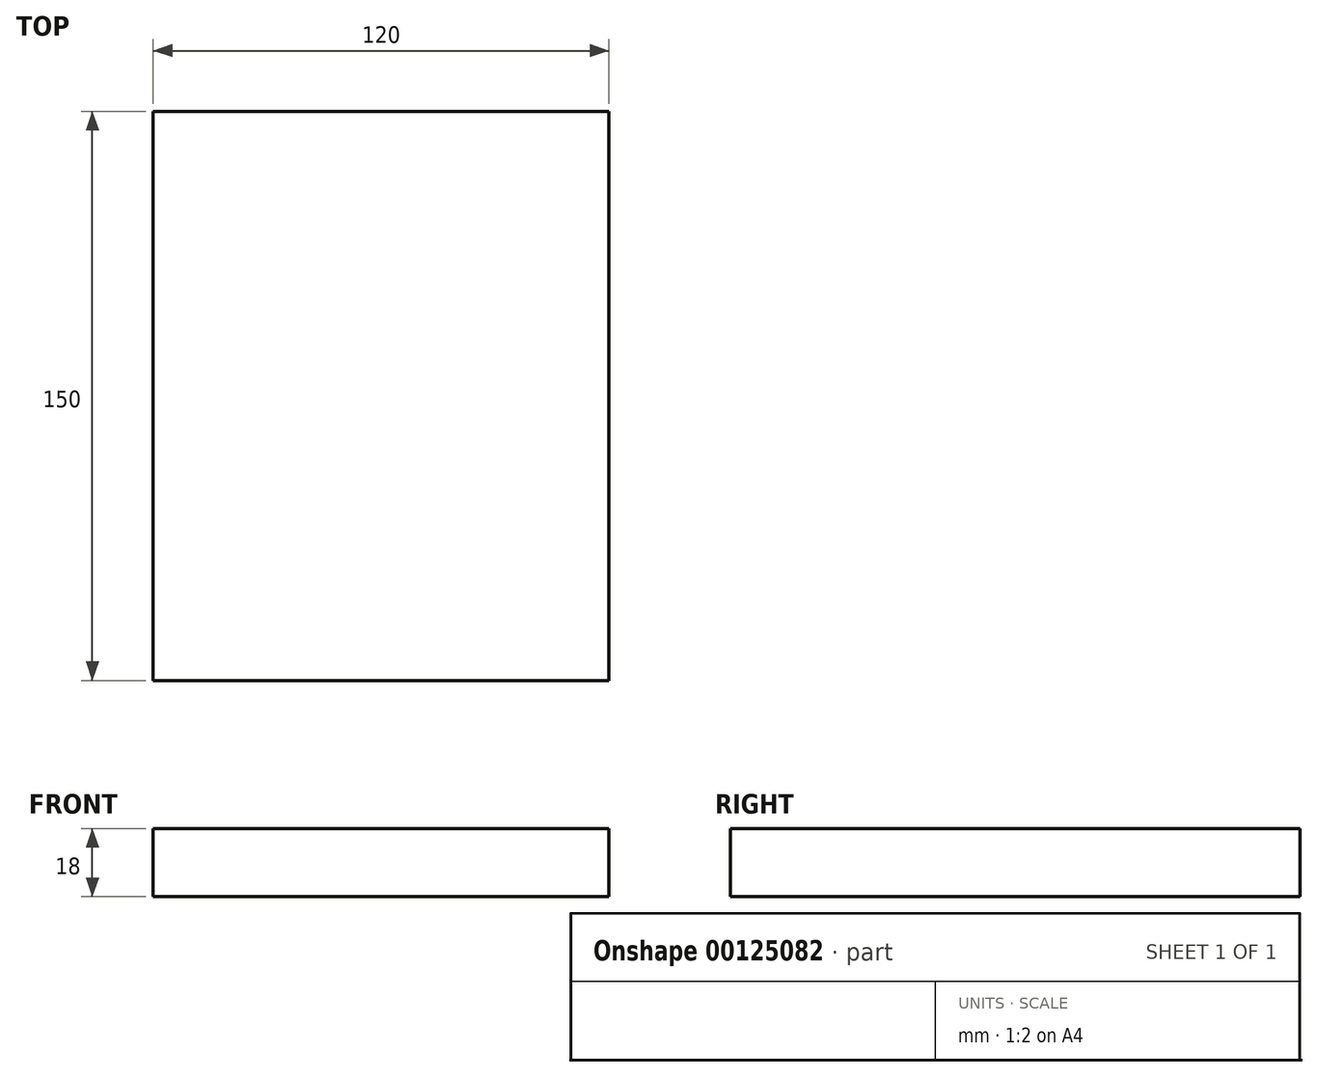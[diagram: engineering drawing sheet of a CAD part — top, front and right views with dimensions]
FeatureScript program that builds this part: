
annotation { "Feature Type Name" : "Feature", "Feature Type Description" : "" }
export const myFeature = defineFeature(function(context is Context, id is Id, definition is map)
    precondition{}
    {
        {
            var Q0;
            Q0=qCreatedBy(makeId("Top.planeOp"),FACE);
            var sketch = newSketch(context, id + "F0", { "sketchPlane" : qUnion([Q0])});
            skLineSegment(sketch, "E0.bottom", {"start": v(0, 0) * mm, "end": v(120, 0) * mm});
            skLineSegment(sketch, "E0.top", {"start": v(0, -150) * mm, "end": v(120, -150) * mm});
            skLineSegment(sketch, "E0.left", {"start": v(0, 0) * mm, "end": v(0, -150) * mm});
            skLineSegment(sketch, "E0.right", {"start": v(120, 0) * mm, "end": v(120, -150) * mm});
            skSolve(sketch);
        }
        {
            var Q0;
            Q0 = qSketchRegion(id + "F0", true);
            var Q1;
            Q1=makeQuery(id+"F0.imprint","IMPRINT",FACE,{"disambiguationData":[TD([[makeQuery(id+"F0.imprint","IMPRINT",EDGE,{"derivedFrom":sQuery(id+"F0.wireOp",EDGE,"E0.bottom")}),-1.0]])]});
            extrude(context, id + "F1", {"entities" : qUnion([Q0, Q1]), "depth" : 18 * mm});
        }
    });
